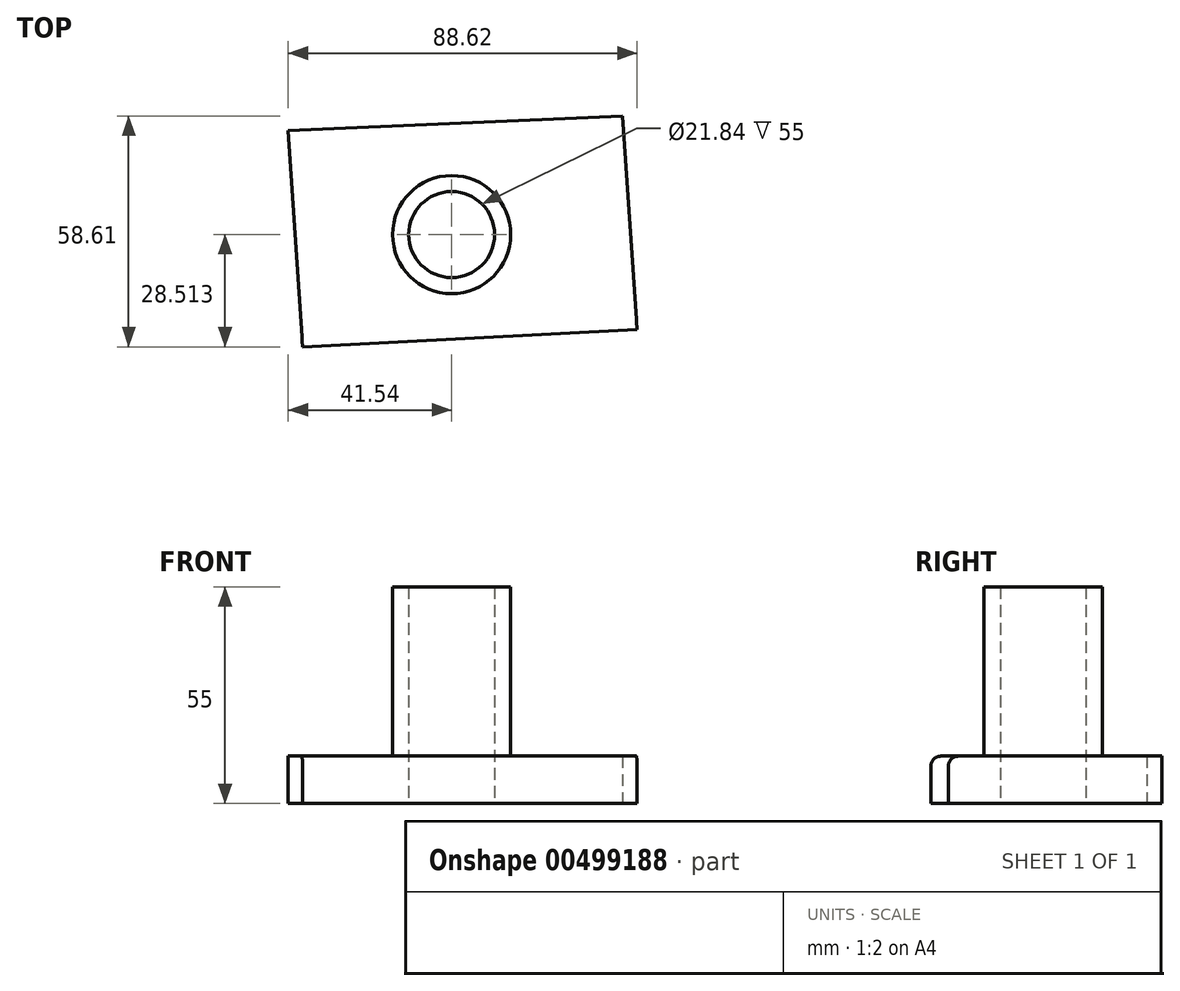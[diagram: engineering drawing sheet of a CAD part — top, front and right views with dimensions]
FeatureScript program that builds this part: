
annotation { "Feature Type Name" : "Feature", "Feature Type Description" : "" }
export const myFeature = defineFeature(function(context is Context, id is Id, definition is map)
    precondition{}
    {
        {
            var Q0;
            Q0=qCreatedBy(makeId("Top.planeOp"),FACE);
            var sketch = newSketch(context, id + "F0", { "sketchPlane" : qUnion([Q0])});
            skLineSegment(sketch, "E0", {"start": v(-41.54, 37.36) * mm, "end": v(43.46, 41.1) * mm});
            skLineSegment(sketch, "E1", {"start": v(43.46, 41.1) * mm, "end": v(47.08, -13.1) * mm});
            skLineSegment(sketch, "E2", {"start": v(47.08, -13.1) * mm, "end": v(-37.9, -17.52) * mm});
            skLineSegment(sketch, "E3", {"start": v(-37.9, -17.52) * mm, "end": v(-41.54, 37.36) * mm});
            skCircle(sketch, "E4", {"center": v(0, 11) * mm, "radius": 15 * mm});
            skCircle(sketch, "E5", {"center": v(0, 11) * mm, "radius": 10.92 * mm});
            skSolve(sketch);
        }
        {
            var Q0;
            Q0=makeQuery(id+"F0.imprint","IMPRINT",FACE,{"disambiguationData":[TD([[makeQuery(id+"F0.imprint","IMPRINT",EDGE,{"derivedFrom":sQuery(id+"F0.wireOp",EDGE,"E0")}),-1.0]])]});
            extrude(context, id + "F1", {"entities" : qUnion([Q0]), "depth" : 12 * mm});
        }
        {
            var Q0;
            Q0=makeQuery(id+"F0.imprint","IMPRINT",FACE,{"disambiguationData":[TD([[makeQuery(id+"F0.imprint","IMPRINT",EDGE,{"derivedFrom":sQuery(id+"F0.wireOp",EDGE,"E4")}),1.0]])]});
            extrude(context, id + "F2", {"entities" : qUnion([Q0]), "operationType" : NewBodyOperationType.ADD, "depth" : 55 * mm});
        }
        {
            var Q0;
            Q0=makeQuery(id+"F1.opExtrude","CAP_EDGE",EDGE,{"disambiguationData":[OSD([sQuery(id+"F0.wireOp",EDGE,"E2")])],"isStart":false});
            fillet(context, id + "F3", {"entities" : qUnion([Q0]), "radius" : 2.5 * mm, "tangentPropagation" : true, "allowEdgeOverflow" : false});
        }
    });
